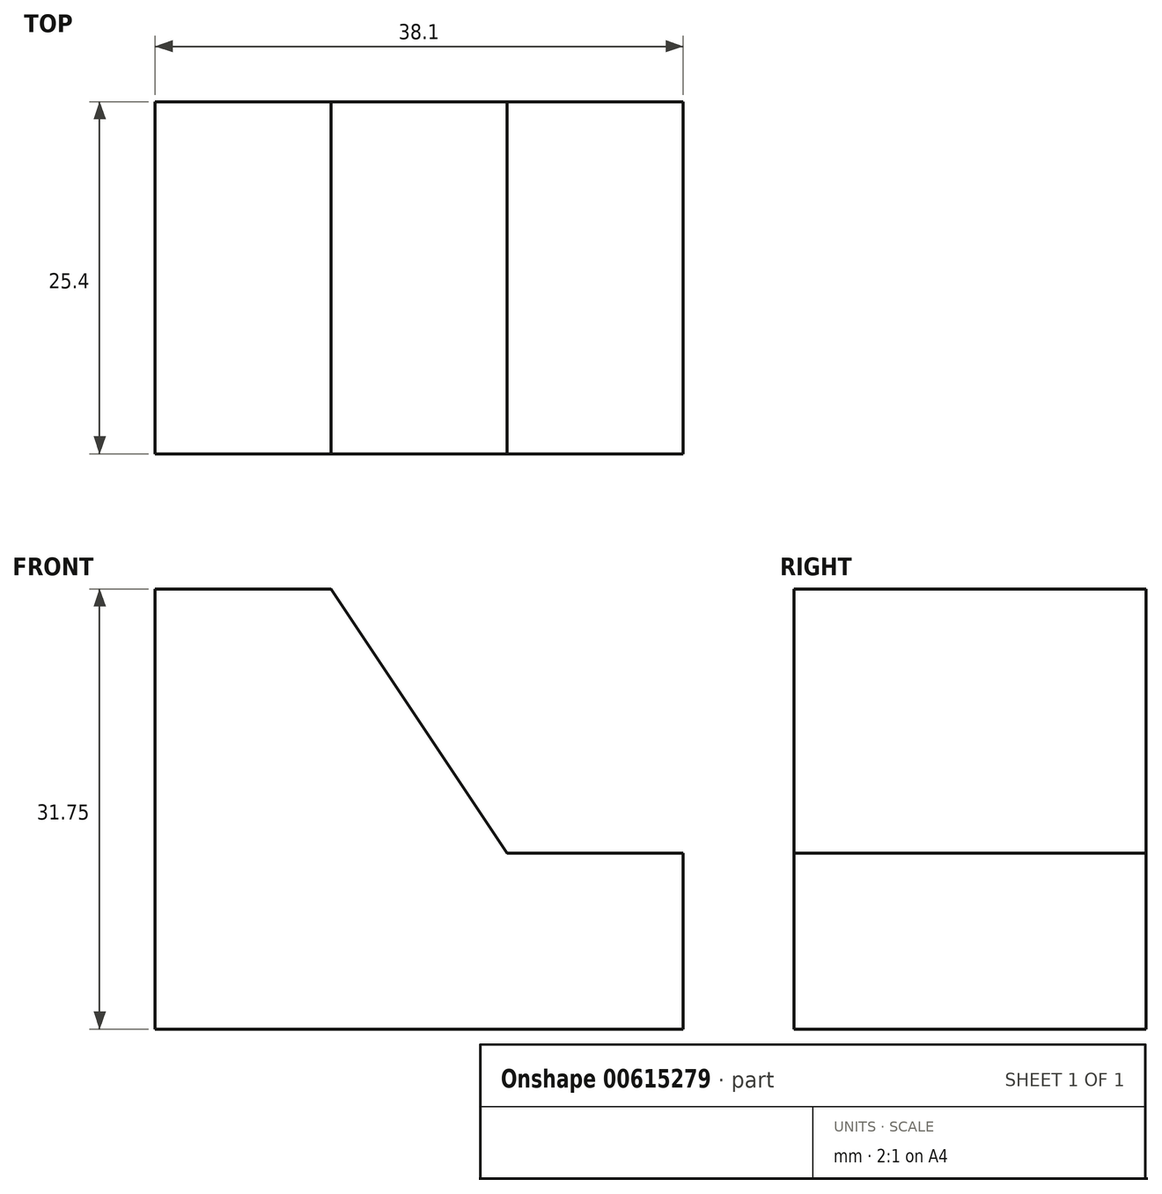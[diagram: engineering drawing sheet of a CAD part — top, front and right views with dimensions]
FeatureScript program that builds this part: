
annotation { "Feature Type Name" : "Feature", "Feature Type Description" : "" }
export const myFeature = defineFeature(function(context is Context, id is Id, definition is map)
    precondition{}
    {
        {
            var Q0;
            Q0=qCreatedBy(makeId("Front.planeOp"),FACE);
            var sketch = newSketch(context, id + "F0", { "sketchPlane" : qUnion([Q0])});
            skLineSegment(sketch, "E0", {"start": v(0, 0) * mm, "end": v(38.1, 0) * mm});
            skLineSegment(sketch, "E1", {"start": v(38.1, 0) * mm, "end": v(38.1, 12.7) * mm});
            skLineSegment(sketch, "E2", {"start": v(38.1, 12.7) * mm, "end": v(25.4, 12.7) * mm});
            skLineSegment(sketch, "E3", {"start": v(0, 0) * mm, "end": v(0, 31.75) * mm});
            skLineSegment(sketch, "E4", {"start": v(0, 31.75) * mm, "end": v(12.7, 31.75) * mm});
            skLineSegment(sketch, "E5", {"start": v(25.4, 12.7) * mm, "end": v(12.7, 31.75) * mm});
            skLineSegment(sketch, "E6", {"start": v(25.4, 12.7) * mm, "end": v(25.4, 0) * mm});
            skSolve(sketch);
        }
        {
            var Q0;
            Q0 = qSketchRegion(id + "F0", true);
            extrude(context, id + "F1", {"entities" : qUnion([Q0]), "depth" : 25.4 * mm, "offsetDistance" : 25.4 * mm});
        }
    });
